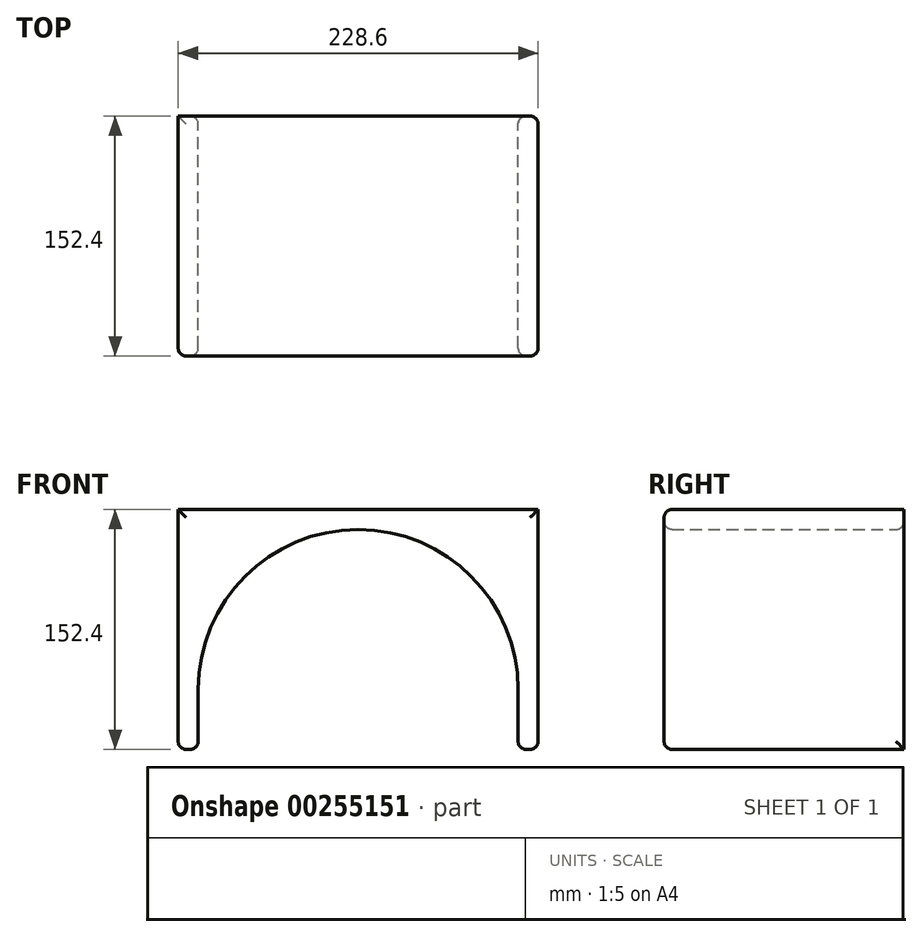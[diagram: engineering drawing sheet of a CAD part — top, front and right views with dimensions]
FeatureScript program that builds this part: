
annotation { "Feature Type Name" : "Feature", "Feature Type Description" : "" }
export const myFeature = defineFeature(function(context is Context, id is Id, definition is map)
    precondition{}
    {
        {
            var Q0;
            Q0=qCreatedBy(makeId("Front.planeOp"),FACE);
            var sketch = newSketch(context, id + "F0", { "sketchPlane" : qUnion([Q0])});
            skArc(sketch, "E0", {"start": v(228.6, 0) * mm, "mid": v(114.3, 114.3) * mm, "end": v(0, 0) * mm});
            skArc(sketch, "E1.0", {"start": v(215.9, 0) * mm, "mid": v(114.3, 101.6) * mm, "end": v(12.7, 0) * mm});
            skLineSegment(sketch, "E2", {"start": v(12.7, 0) * mm, "end": v(12.7, -38.1) * mm});
            skLineSegment(sketch, "E3", {"start": v(215.9, 0) * mm, "end": v(215.9, -38.1) * mm});
            skLineSegment(sketch, "E4", {"start": v(228.6, 0) * mm, "end": v(228.6, -38.1) * mm});
            skLineSegment(sketch, "E5", {"start": v(0, -38.1) * mm, "end": v(12.7, -38.1) * mm});
            skLineSegment(sketch, "E6", {"start": v(215.9, -38.1) * mm, "end": v(228.6, -38.1) * mm});
            skLineSegment(sketch, "E7", {"start": v(114.3, 114.3) * mm, "end": v(0, 114.3) * mm});
            skLineSegment(sketch, "E8", {"start": v(0, -38.1) * mm, "end": v(0, 114.3) * mm});
            skPoint(sketch, "E9.orphan", {"position": v(0, -76.2) * mm});
            skPoint(sketch, "E10.end.orphan", {"position": v(-12.7, -38.1) * mm});
            skPoint(sketch, "E11.center.orphan", {"position": v(-114.3, 0) * mm});
            skPoint(sketch, "E11.start.orphan", {"position": v(-114.3, 114.3) * mm});
            skPoint(sketch, "E12.start.orphan", {"position": v(-228.6, 0) * mm});
            skPoint(sketch, "E13.start.orphan", {"position": v(-215.9, 0) * mm});
            skPoint(sketch, "E14.end.orphan", {"position": v(-215.9, -38.1) * mm});
            skPoint(sketch, "E14.start.orphan", {"position": v(-228.6, -38.1) * mm});
            skLineSegment(sketch, "E15", {"start": v(114.3, 114.3) * mm, "end": v(228.6, 114.3) * mm});
            skLineSegment(sketch, "E16", {"start": v(228.6, 114.3) * mm, "end": v(228.6, 0) * mm});
            skSolve(sketch);
        }
        {
            var Q0;
            Q0 = qSketchRegion(id + "F0", true);
            extrude(context, id + "F1", {"entities" : qUnion([Q0]), "depth" : 152.4 * mm});
        }
        {
            var Q0;
            Q0=makeQuery(id+"F1.opExtrude","CAP_EDGE",EDGE,{"disambiguationData":[OSD([sQuery(id+"F0.wireOp",EDGE,"2a9f6da4-7894-4758-9daf-b3bd383070b8.0")])],"isStart":false});
            var Q1;
            Q1=makeQuery(id+"F1.opExtrude","CAP_EDGE",EDGE,{"disambiguationData":[OSD([sQuery(id+"F0.wireOp",EDGE,"E1.0")])],"isStart":false});
            var Q2;
            Q2=makeQuery(id+"F1.opExtrude","CAP_EDGE",EDGE,{"disambiguationData":[OSD([sQuery(id+"F0.wireOp",EDGE,"E1.0")])],"isStart":true});
            var Q3;
            Q3=makeQuery(id+"F1.opExtrude","CAP_EDGE",EDGE,{"disambiguationData":[OSD([sQuery(id+"F0.wireOp",EDGE,"2a9f6da4-7894-4758-9daf-b3bd383070b8.0")])],"isStart":true});
            var Q4;
            Q4=makeQuery(id+"F1.opExtrude","CAP_EDGE",EDGE,{"disambiguationData":[OSD([sQuery(id+"F0.wireOp",EDGE,"E6")])],"isStart":false});
            var Q5;
            Q5=makeQuery(id+"F1.opExtrude","CAP_EDGE",EDGE,{"disambiguationData":[OSD([sQuery(id+"F0.wireOp",EDGE,"E5")])],"isStart":false});
            var Q6;
            Q6=makeQuery(id+"F1.opExtrude","SWEPT_EDGE",EDGE,{"disambiguationData":[OSD([sQuery(id+"F0.wireOp",EDGE,"E10"),sQuery(id+"F0.wireOp",EDGE,"E5")])]});
            var Q7;
            Q7=makeQuery(id+"F1.opExtrude","SWEPT_EDGE",EDGE,{"disambiguationData":[OSD([sQuery(id+"F0.wireOp",EDGE,"E2"),sQuery(id+"F0.wireOp",EDGE,"E5")])]});
            var Q8;
            Q8=makeQuery(id+"F1.opExtrude","SWEPT_FACE",FACE,{"disambiguationData":[OSD([sQuery(id+"F0.wireOp",EDGE,"E5")])]});
            var Q9;
            Q9=makeQuery(id+"F1.opExtrude","CAP_EDGE",EDGE,{"disambiguationData":[OSD([sQuery(id+"F0.wireOp",EDGE,"E14")])],"isStart":false});
            var Q10;
            Q10=makeQuery(id+"F1.opExtrude","SWEPT_EDGE",EDGE,{"disambiguationData":[OSD([sQuery(id+"F0.wireOp",EDGE,"E3"),sQuery(id+"F0.wireOp",EDGE,"E6")])]});
            var Q11;
            Q11=makeQuery(id+"F1.opExtrude","SWEPT_EDGE",EDGE,{"disambiguationData":[OSD([sQuery(id+"F0.wireOp",EDGE,"E13"),sQuery(id+"F0.wireOp",EDGE,"E14")])]});
            fillet(context, id + "F2", {"entities" : qUnion([Q0, Q1, Q2, Q3, Q4, Q5, Q6, Q7, Q8, Q9, Q10, Q11]), "radius" : 5.08 * mm, "tangentPropagation" : true, "allowEdgeOverflow" : false});
        }
        {
            var Q0;
            Q0=makeQuery(id+"F1.opExtrude","CAP_EDGE",EDGE,{"disambiguationData":[OSD([sQuery(id+"F0.wireOp",EDGE,"E4"),sQuery(id+"F0.wireOp",EDGE,"E16")])],"isStart":false});
            var Q1;
            Q1=makeQuery(id+"F1.opExtrude","CAP_EDGE",EDGE,{"disambiguationData":[OSD([sQuery(id+"F0.wireOp",EDGE,"E7"),sQuery(id+"F0.wireOp",EDGE,"E15")])],"isStart":false});
            var Q2;
            Q2=makeQuery(id+"F1.opExtrude","CAP_EDGE",EDGE,{"disambiguationData":[OSD([sQuery(id+"F0.wireOp",EDGE,"E8")])],"isStart":false});
            var Q3;
            Q3=makeQuery(id+"F1.opExtrude","CAP_EDGE",EDGE,{"disambiguationData":[OSD([sQuery(id+"F0.wireOp",EDGE,"E4"),sQuery(id+"F0.wireOp",EDGE,"E16")])],"isStart":true});
            fillet(context, id + "F3", {"entities" : qUnion([Q0, Q1, Q2, Q3]), "radius" : 5.08 * mm, "tangentPropagation" : true, "allowEdgeOverflow" : false});
        }
    });
